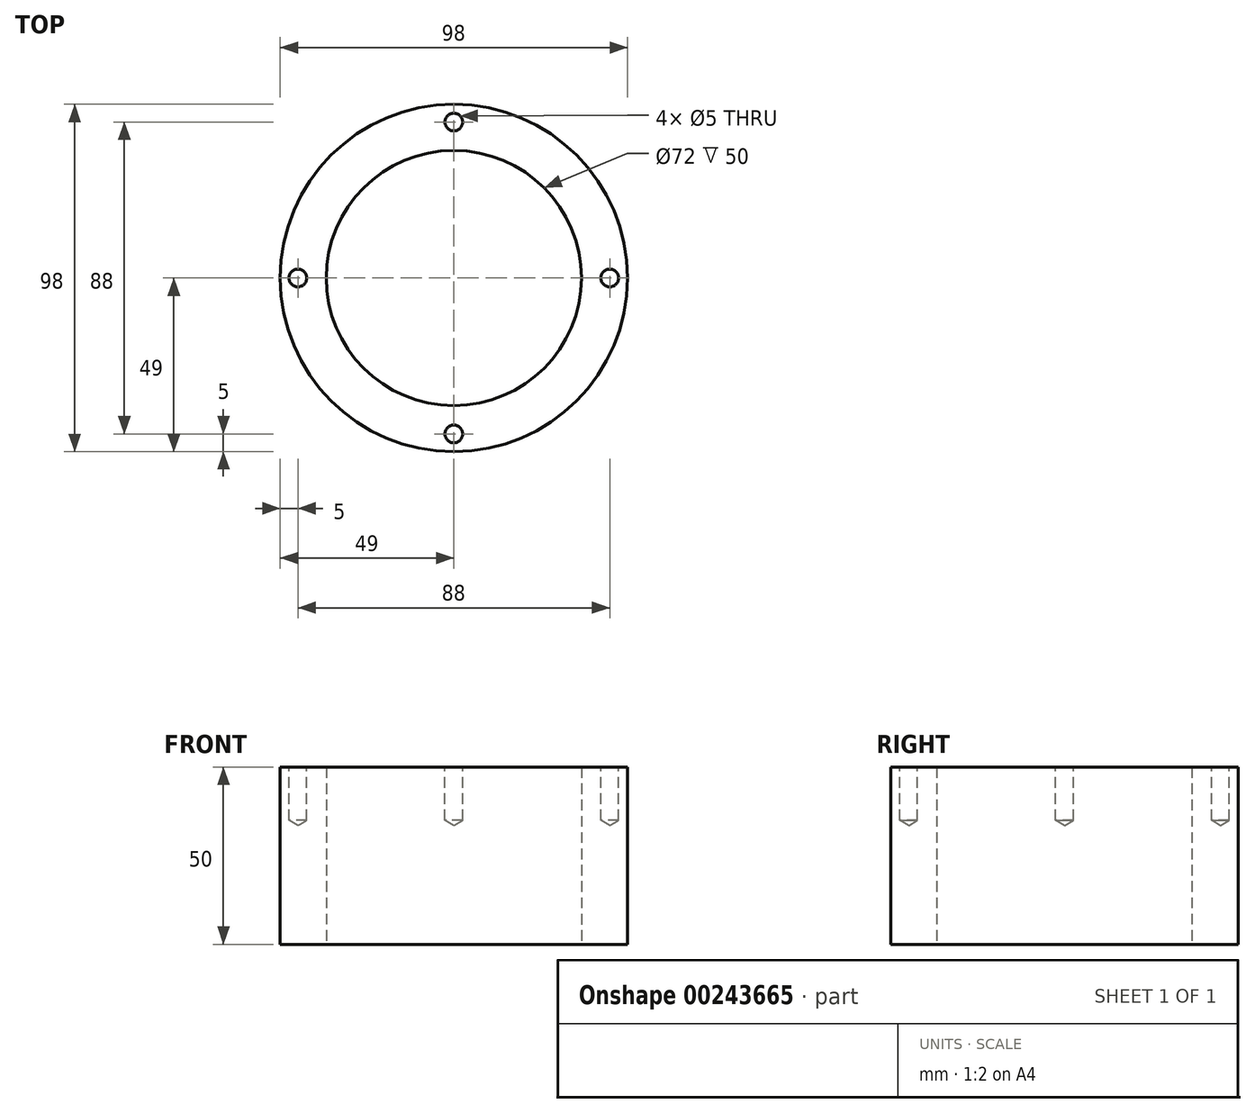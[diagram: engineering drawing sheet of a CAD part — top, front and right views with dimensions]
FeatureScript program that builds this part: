
annotation { "Feature Type Name" : "Feature", "Feature Type Description" : "" }
export const myFeature = defineFeature(function(context is Context, id is Id, definition is map)
    precondition{}
    {
        {
            var Q0;
            Q0=qCreatedBy(makeId("Top.planeOp"),FACE);
            var sketch = newSketch(context, id + "F0", { "sketchPlane" : qUnion([Q0])});
            skCircle(sketch, "E0", {"center": v(0, 0) * mm, "radius": 49 * mm});
            skCircle(sketch, "E1", {"center": v(0, 0) * mm, "radius": 36 * mm});
            skSolve(sketch);
        }
        {
            var Q0;
            Q0 = qSketchRegion(id + "F0", true);
            extrude(context, id + "F1", {"entities" : qUnion([Q0]), "endBound" : BoundingType.SYMMETRIC, "depth" : 50 * mm});
        }
        {
            var Q0;
            Q0=makeQuery(id+"F1.opExtrude","CAP_FACE",FACE,{"disambiguationData":[OSD([sQuery(id+"F0.wireOp",EDGE,"E0"),sQuery(id+"F0.wireOp",EDGE,"E1")])],"isStart":false});
            var sketch = newSketch(context, id + "F2", { "sketchPlane" : qUnion([Q0])});
            skCircle(sketch, "E2", {"center": v(0, 0) * mm, "radius": 44 * mm, "construction": true});
            skLineSegment(sketch, "E3", {"start": v(0, 0) * mm, "end": v(0, -44) * mm, "construction": true});
            skLineSegment(sketch, "E4", {"start": v(0, 0) * mm, "end": v(0, 44) * mm, "construction": true});
            skLineSegment(sketch, "E5", {"start": v(0, 0) * mm, "end": v(44, 0) * mm, "construction": true});
            skLineSegment(sketch, "E6", {"start": v(0, 0) * mm, "end": v(-44, 0) * mm, "construction": true});
            skSolve(sketch);
        }
        {
            var Q0;
            Q0=sQuery(id+"F2.wireOp",VERTEX,"E4.end");
            var Q1;
            Q1=sQuery(id+"F2.wireOp",VERTEX,"E6.end");
            var Q2;
            Q2=sQuery(id+"F2.wireOp",VERTEX,"E3.end");
            var Q3;
            Q3=sQuery(id+"F2.wireOp",VERTEX,"E5.end");
            var Q4;
            Q4=makeQuery(id+"F1.opExtrude","SWEPT_BODY",BODY,{"disambiguationData":[OSD([sQuery(id+"F0.wireOp",EDGE,"E0"),sQuery(id+"F0.wireOp",EDGE,"E1")])]});
            hole(context, id + "F3", {"style" : HoleStyle.SIMPLE, "endStyle" : HoleEndStyle.BLIND, "holeDiameter" : 5 * mm, "holeDepth" : 15 * mm, "tappedDepth" : 12.7 * mm, "tapClearance" : 3, "locations" : qUnion([Q0, Q1, Q2, Q3]), "scope" : qUnion([Q4])});
        }
    });
